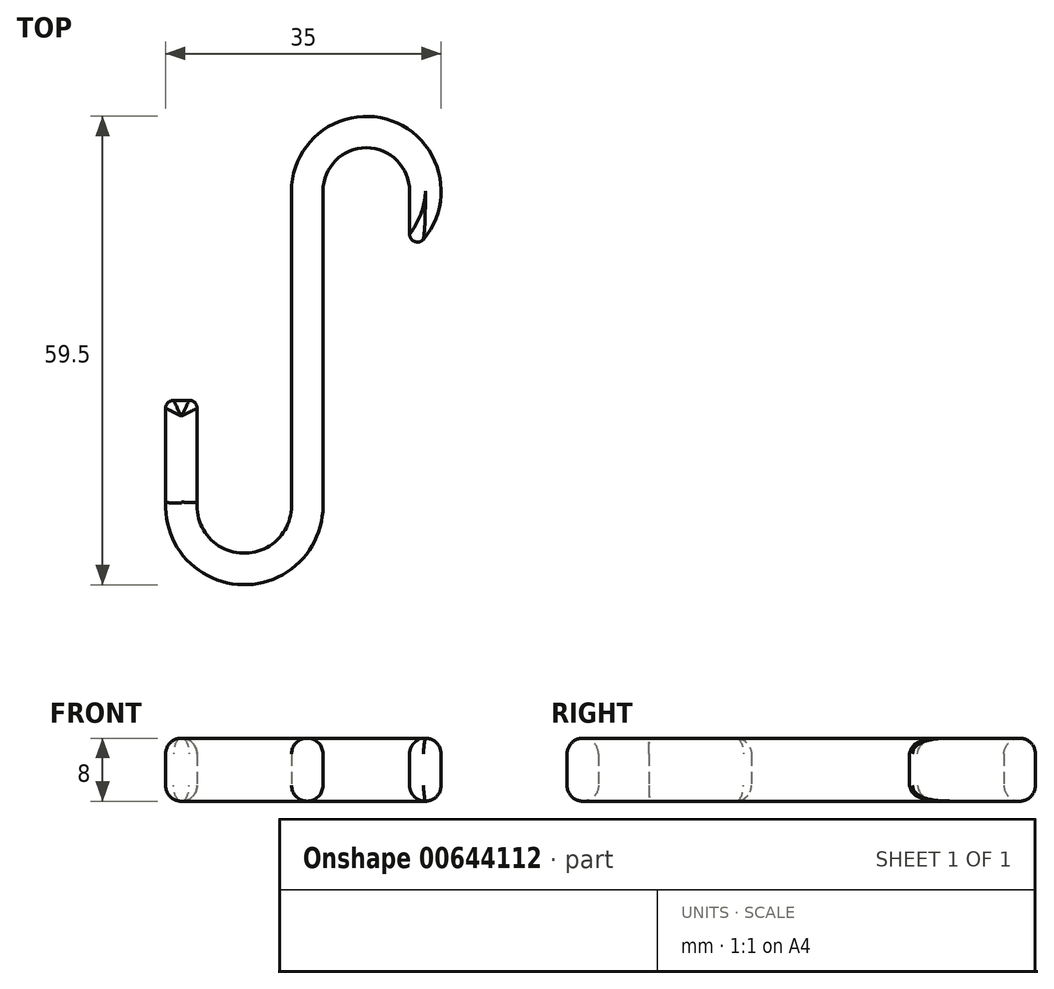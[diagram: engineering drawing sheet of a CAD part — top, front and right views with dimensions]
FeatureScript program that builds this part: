
annotation { "Feature Type Name" : "Feature", "Feature Type Description" : "" }
export const myFeature = defineFeature(function(context is Context, id is Id, definition is map)
    precondition{}
    {
        {
            var Q0;
            Q0=qCreatedBy(makeId("Top.planeOp"),FACE);
            var sketch = newSketch(context, id + "F0", { "sketchPlane" : qUnion([Q0])});
            skArc(sketch, "E0", {"start": v(5.5, 0) * mm, "mid": v(0, 5.5) * mm, "end": v(-5.5, 0) * mm});
            skArc(sketch, "E1", {"start": v(-21.49, -39.58) * mm, "mid": v(-15.71, -46) * mm, "end": v(-9.5, -40) * mm});
            skArc(sketch, "E2.0", {"start": v(5.5, -7.75) * mm, "mid": v(4.36, 8.44) * mm, "end": v(-9.5, 0) * mm});
            skLineSegment(sketch, "E3", {"start": v(-9.5, 0) * mm, "end": v(-9.5, -41.8) * mm, "construction": true});
            skArc(sketch, "E4.0", {"start": v(-25.5, -39.58) * mm, "mid": v(-15.71, -50) * mm, "end": v(-5.5, -40) * mm});
            skLineSegment(sketch, "E5", {"start": v(-5.5, 0) * mm, "end": v(-5.5, -40) * mm});
            skLineSegment(sketch, "E6", {"start": v(-9.5, 0) * mm, "end": v(-9.5, -32) * mm});
            skLineSegment(sketch, "E7", {"start": v(-25.5, -39.58) * mm, "end": v(-25.5, -26.58) * mm});
            skLineSegment(sketch, "E8", {"start": v(-21.49, -39.58) * mm, "end": v(-21.49, -26.58) * mm});
            skLineSegment(sketch, "E9", {"start": v(-21.49, -26.58) * mm, "end": v(-25.5, -26.58) * mm});
            skLineSegment(sketch, "E10", {"start": v(-9.5, -32) * mm, "end": v(-9.5, -40) * mm});
            skLineSegment(sketch, "E11", {"start": v(5.5, 0) * mm, "end": v(5.5, -7.75) * mm});
            skSolve(sketch);
        }
        {
            var Q0;
            Q0=qSketchRegion(id+"F0",true);
            extrude(context, id + "F1", {"entities" : qUnion([Q0]), "depth" : 8 * mm, "offsetDistance" : 25 * mm});
        }
        {
            var Q0;
            Q0=makeQuery(id+"F1.opExtrude","CAP_FACE",FACE,{"disambiguationData":[OSD([sQuery(id+"F0.wireOp",EDGE,"E0"),sQuery(id+"F0.wireOp",EDGE,"E1"),sQuery(id+"F0.wireOp",EDGE,"E2.0"),sQuery(id+"F0.wireOp",EDGE,"E4.0"),sQuery(id+"F0.wireOp",EDGE,"E5"),sQuery(id+"F0.wireOp",EDGE,"E6"),sQuery(id+"F0.wireOp",EDGE,"E7"),sQuery(id+"F0.wireOp",EDGE,"E8"),sQuery(id+"F0.wireOp",EDGE,"E9"),sQuery(id+"F0.wireOp",EDGE,"E10"),sQuery(id+"F0.wireOp",EDGE,"E11")])],"isStart":false});
            var Q1;
            Q1=makeQuery(id+"F1.opExtrude","CAP_FACE",FACE,{"disambiguationData":[OSD([sQuery(id+"F0.wireOp",EDGE,"E0"),sQuery(id+"F0.wireOp",EDGE,"E1"),sQuery(id+"F0.wireOp",EDGE,"E2.0"),sQuery(id+"F0.wireOp",EDGE,"E4.0"),sQuery(id+"F0.wireOp",EDGE,"E5"),sQuery(id+"F0.wireOp",EDGE,"E6"),sQuery(id+"F0.wireOp",EDGE,"E7"),sQuery(id+"F0.wireOp",EDGE,"E8"),sQuery(id+"F0.wireOp",EDGE,"E9"),sQuery(id+"F0.wireOp",EDGE,"E10"),sQuery(id+"F0.wireOp",EDGE,"E11")])],"isStart":true});
            fillet(context, id + "F2", {"entities" : qUnion([Q0, Q1]), "radius" : 2 * mm, "tangentPropagation" : true, "allowEdgeOverflow" : false});
        }
        {
            var Q0;
            Q0=makeQuery(id+"F1.opExtrude","SWEPT_FACE",FACE,{"disambiguationData":[OSD([sQuery(id+"F0.wireOp",EDGE,"E9")])]});
            fillet(context, id + "F3", {"entities" : qUnion([Q0]), "radius" : 1 * mm, "tangentPropagation" : true, "allowEdgeOverflow" : false});
        }
        {
            var Q0;
            Q0=makeQuery(id+"F1.opExtrude","SWEPT_EDGE",EDGE,{"disambiguationData":[OSD([sQuery(id+"F0.wireOp",EDGE,"E2.0"),sQuery(id+"F0.wireOp",EDGE,"E11")])]});
            var Q1;
            Q1=makeQuery(id+"F2.opFillet","BLEND_EDGE",EDGE,{"blendedFrom":[makeQuery(id+"F1.opExtrude","CAP_EDGE",EDGE,{"disambiguationData":[OSD([sQuery(id+"F0.wireOp",EDGE,"E2.0")])],"isStart":false}),makeQuery(id+"F1.opExtrude","CAP_EDGE",EDGE,{"disambiguationData":[OSD([sQuery(id+"F0.wireOp",EDGE,"E11")])],"isStart":false})],"blendedInto":[]});
            var Q2;
            Q2=makeQuery(id+"F2.opFillet","BLEND_EDGE",EDGE,{"blendedFrom":[makeQuery(id+"F1.opExtrude","CAP_EDGE",EDGE,{"disambiguationData":[OSD([sQuery(id+"F0.wireOp",EDGE,"E2.0")])],"isStart":true}),makeQuery(id+"F1.opExtrude","CAP_EDGE",EDGE,{"disambiguationData":[OSD([sQuery(id+"F0.wireOp",EDGE,"E11")])],"isStart":true})],"blendedInto":[]});
            fillet(context, id + "F4", {"entities" : qUnion([Q0, Q1, Q2]), "radius" : 1 * mm, "tangentPropagation" : true, "allowEdgeOverflow" : false});
        }
    });
